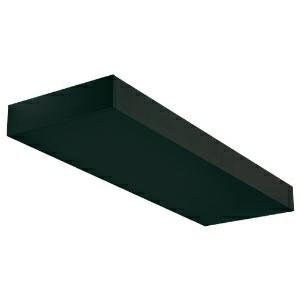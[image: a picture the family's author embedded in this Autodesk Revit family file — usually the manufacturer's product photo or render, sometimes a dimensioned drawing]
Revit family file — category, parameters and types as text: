
# Revit family: speed_wall_uplight_310-4210
name_source: partatom
category: Lighting Fixtures
units: mm (PartAtom-declared; Revit-internal decimal feet)

## family parameters
Cut with Voids When Loaded = No
Host = Face
Light Source = No
Part Type = Normal
Room Calculation Point = No
Round Connector Dimension = Use Diameter
Shared = No

## types (1)
- 310-4210-F01-S27 (4 x LED, 1310 lm, 8.6 W, 2700K)
    Apparent Load = 34 VA
    CIE Flux Codes = 0 0 0 0 83
    Color Rendering = 1B/80…89
    Color Temperature = 2700K
    Default Elevation = 1800 mm
    Description = SPEED WALL UPLIGHT
    Height = 50 mm
    Lamp = 4 x LED
    Lamp Light Flux = 1310 lm
    Lamp Power = 8.6 W
    Lamp count = 4
    Length = 605 mm
    Luminous efficacy = 127 lm/W
    Manufacturer = Prolicht
    ModVariant = No
    Model = 310-4210
    Mounting Place = Ceiling
    Mounting Type = Surface mounted
    Number of Poles = 1
    OnlyDefault = Yes
    Power Factor = 1
    Product Name = SPEED WALL UPLIGHT
    Product group = Surface lights
    ProductGroupID = 331
    Protection Class = Protection class
    Protection Degree = Degree of protection
    RLX_Detail_Level = 1
    RLX_Emergency_Light_Flux = 0 lm
    RLX_Emergency_Type = 0
    RLX_Emergency_Type_DB = No
    RlxData = <blob elided: 71857 chars, md5=df4e3350>
    Socket = socket
    Standby Power = 0 W
    System Light Flux = 4370 lm
    System Power = 34 W
    Type Comments = DIFFUSER INDIRECT Opal (01),LED COLOUR IND 2700 K (27)
    Type Image = 310-4210.jpg
    URL = http://relux.com
    VarID = 310-4210-f01-s27
    Voltage = 0 V
    Weight = 0.00 kg
    Width = 195 mm

## geometry (parser evidence)
native form markers: Blend x4, Sweep x12
no freeform markers — native parametric forms only
